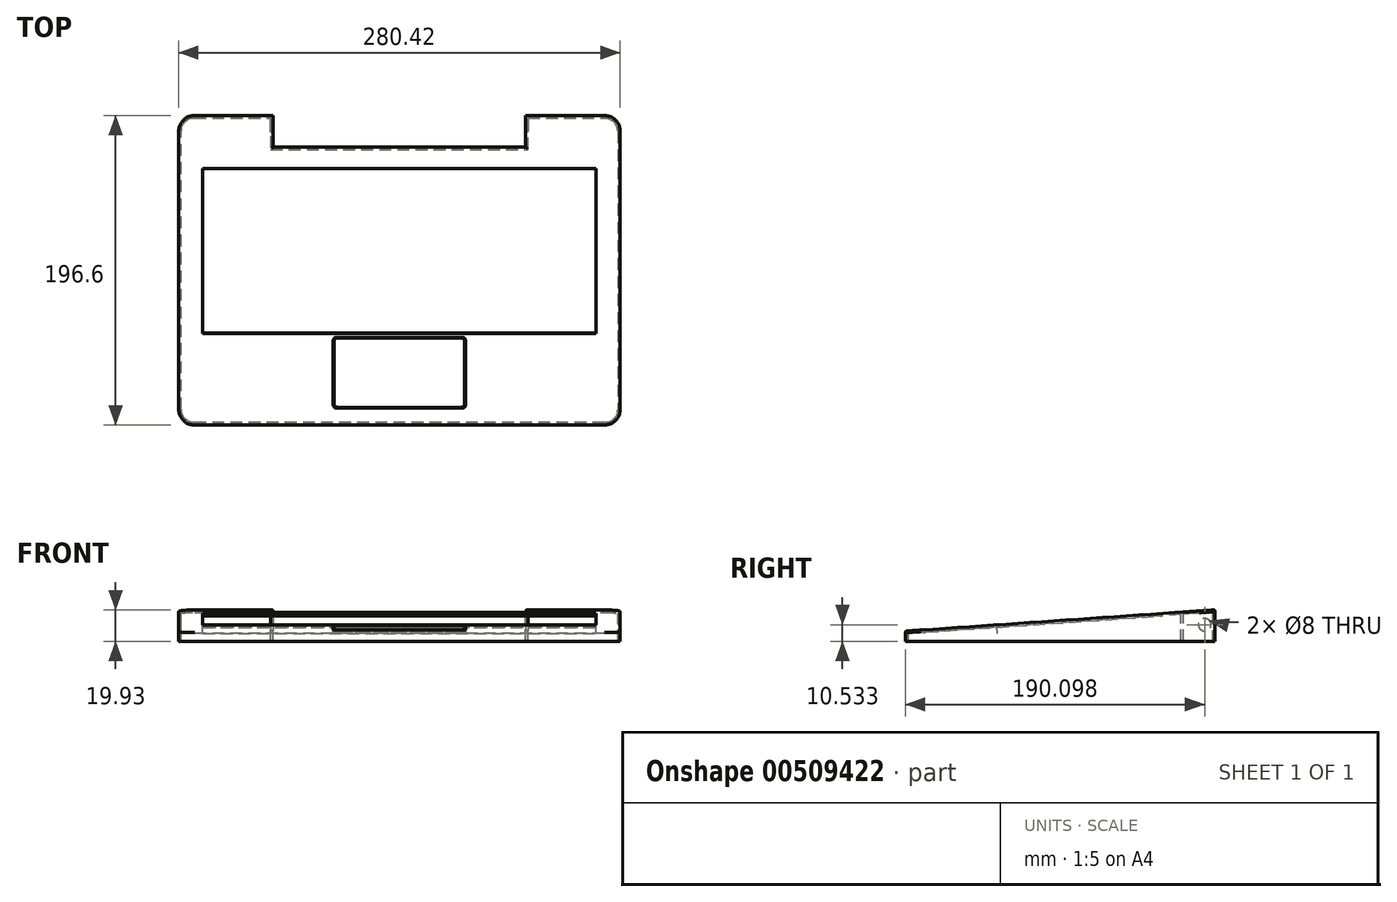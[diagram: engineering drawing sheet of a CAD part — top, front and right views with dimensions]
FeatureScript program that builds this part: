
annotation { "Feature Type Name" : "Feature", "Feature Type Description" : "" }
export const myFeature = defineFeature(function(context is Context, id is Id, definition is map)
    precondition{}
    {
        {
            var Q0;
            Q0=qCreatedBy(makeId("Right.planeOp"),FACE);
            cPlane(context, id + "F0", {"entities" : qUnion([Q0]), "cplaneType" : CPlaneType.OFFSET, "offset" : 140.2 * mm, "oppositeDirection" : true, "width" : 150 * mm, "height" : 150 * mm});
        }
        {
            var Q0;
            Q0=qCreatedBy(id+"F0.planeOp",FACE);
            var sketch = newSketch(context, id + "F1", { "sketchPlane" : qUnion([Q0])});
            skLineSegment(sketch, "E0.bottom", {"start": v(-98.3, -10) * mm, "end": v(98.3, -10) * mm});
            skLineSegment(sketch, "E0.right", {"start": v(98.3, -10) * mm, "end": v(98.3, 10) * mm});
            skPoint(sketch, "E0.middle", {"position": v(0, 0) * mm});
            skPoint(sketch, "E1", {"position": v(98.3, 0) * mm});
            skPoint(sketch, "E2", {"position": v(0, -10) * mm});
            skLineSegment(sketch, "E3", {"start": v(-98.3, -10) * mm, "end": v(-98.3, -3.5) * mm});
            skLineSegment(sketch, "E4", {"start": v(98.3, 10) * mm, "end": v(-98.3, -3.5) * mm});
            skSolve(sketch);
        }
        {
            var Q0;
            Q0=makeQuery(id+"F1.imprint","IMPRINT",FACE,{"disambiguationData":[TD([[makeQuery(id+"F1.imprint","IMPRINT",EDGE,{"derivedFrom":sQuery(id+"F1.wireOp",EDGE,"E0.bottom")}),1.0]])]});
            extrude(context, id + "F2", {"entities" : qUnion([Q0]), "depth" : 280.42 * mm, "offsetDistance" : 25 * mm});
        }
        {
            var Q0;
            Q0=makeQuery(id+"F2.opExtrude","CAP_EDGE",EDGE,{"disambiguationData":[OSD([sQuery(id+"F1.wireOp",EDGE,"E0.right")])],"isStart":true});
            var Q1;
            Q1=makeQuery(id+"F2.opExtrude","CAP_EDGE",EDGE,{"disambiguationData":[OSD([sQuery(id+"F1.wireOp",EDGE,"E3")])],"isStart":true});
            var Q2;
            Q2=makeQuery(id+"F2.opExtrude","CAP_EDGE",EDGE,{"disambiguationData":[OSD([sQuery(id+"F1.wireOp",EDGE,"E3")])],"isStart":false});
            var Q3;
            Q3=makeQuery(id+"F2.opExtrude","CAP_EDGE",EDGE,{"disambiguationData":[OSD([sQuery(id+"F1.wireOp",EDGE,"E0.right")])],"isStart":false});
            fillet(context, id + "F3", {"entities" : qUnion([Q0, Q1, Q2, Q3]), "radius" : 10 * mm, "tangentPropagation" : true, "allowEdgeOverflow" : false});
        }
        {
            var Q0;
            Q0=makeQuery(id+"F2.opExtrude","SWEPT_FACE",FACE,{"disambiguationData":[OSD([sQuery(id+"F1.wireOp",EDGE,"E0.bottom")])]});
            cPlane(context, id + "F4", {"entities" : qUnion([Q0]), "cplaneType" : CPlaneType.OFFSET, "offset" : 26.5 * mm, "oppositeDirection" : true, "width" : 150 * mm, "height" : 150 * mm});
        }
        {
            var Q0;
            Q0=qCreatedBy(id+"F4.planeOp",FACE);
            var sketch = newSketch(context, id + "F5", { "sketchPlane" : qUnion([Q0])});
            skPoint(sketch, "E5", {"position": v(-80.2, -98.3) * mm});
            skPoint(sketch, "E6", {"position": v(80.2, -98.3) * mm});
            skLineSegment(sketch, "E7.bottom", {"start": v(-80.2, -98.3) * mm, "end": v(80.2, -98.3) * mm});
            skLineSegment(sketch, "E7.top", {"start": v(-80.2, -78.3) * mm, "end": v(80.2, -78.3) * mm});
            skLineSegment(sketch, "E7.left", {"start": v(-80.2, -98.3) * mm, "end": v(-80.2, -78.3) * mm});
            skLineSegment(sketch, "E7.right", {"start": v(80.2, -98.3) * mm, "end": v(80.2, -78.3) * mm});
            skSolve(sketch);
        }
        {
            var Q0;
            Q0 = qSketchRegion(id + "F5", true);
            extrude(context, id + "F6", {"entities" : qUnion([Q0]), "operationType" : NewBodyOperationType.REMOVE, "depth" : 30 * mm, "offsetDistance" : 25 * mm});
        }
        {
            var Q0;
            Q0=makeQuery(id+"F2.opExtrude","SWEPT_FACE",FACE,{"disambiguationData":[OSD([sQuery(id+"F1.wireOp",EDGE,"E4")])]});
            fillet(context, id + "F7", {"entities" : qUnion([Q0]), "radius" : 1 * mm, "tangentPropagation" : true, "rho" : 0.5, "crossSection" : FilletCrossSection.CONIC, "allowEdgeOverflow" : false});
        }
        {
            var Q0;
            Q0=makeQuery(id+"F2.opExtrude","SWEPT_FACE",FACE,{"disambiguationData":[OSD([sQuery(id+"F1.wireOp",EDGE,"E0.bottom")])]});
            shell(context, id + "F8", {"entities" : qUnion([Q0]), "thickness" : 1.5 * mm});
        }
        {
            var Q0;
            Q0=makeQuery(id+"F2.opExtrude","SWEPT_FACE",FACE,{"disambiguationData":[OSD([sQuery(id+"F1.wireOp",EDGE,"E4")])]});
            var sketch = newSketch(context, id + "F9", { "sketchPlane" : qUnion([Q0])});
            skLineSegment(sketch, "E8.bottom", {"start": v(125, 65) * mm, "end": v(-125, 65) * mm});
            skPoint(sketch, "E8.middle", {"position": v(0, 0) * mm});
            skPoint(sketch, "E9", {"position": v(0, 65) * mm});
            skLineSegment(sketch, "E10", {"start": v(-125, 65) * mm, "end": v(-125, -40) * mm});
            skLineSegment(sketch, "E11", {"start": v(125, 65) * mm, "end": v(125, -40) * mm});
            skLineSegment(sketch, "E12", {"start": v(-125, -40) * mm, "end": v(125, -40) * mm});
            skPoint(sketch, "E13", {"position": v(0, 12.5) * mm});
            skPoint(sketch, "E13.positionSnap0", {"position": v(-125, 12.5) * mm});
            skSolve(sketch);
        }
        {
            var Q0;
            Q0=makeQuery(id+"F2.opExtrude","SWEPT_FACE",FACE,{"disambiguationData":[OSD([sQuery(id+"F1.wireOp",EDGE,"E4")])]});
            var sketch = newSketch(context, id + "F10", { "sketchPlane" : qUnion([Q0])});
            skPoint(sketch, "E14", {"position": v(0, -65) * mm});
            skLineSegment(sketch, "E15.bottom", {"start": v(40, -87.5) * mm, "end": v(-40, -87.5) * mm});
            skLineSegment(sketch, "E15.top", {"start": v(40, -42.5) * mm, "end": v(-40, -42.5) * mm});
            skLineSegment(sketch, "E15.left", {"start": v(42, -85.5) * mm, "end": v(42, -44.5) * mm});
            skLineSegment(sketch, "E15.right", {"start": v(-42, -85.5) * mm, "end": v(-42, -44.5) * mm});
            skPoint(sketch, "E16.visualSharp", {"position": v(-42, -42.5) * mm});
            skArc(sketch, "E16.filletArc", {"start": v(-40, -42.5) * mm, "mid": v(-41.41, -43.09) * mm, "end": v(-42, -44.5) * mm});
            skPoint(sketch, "E17.visualSharp", {"position": v(42, -42.5) * mm});
            skArc(sketch, "E17.filletArc", {"start": v(42, -44.5) * mm, "mid": v(41.41, -43.09) * mm, "end": v(40, -42.5) * mm});
            skPoint(sketch, "E18.visualSharp", {"position": v(42, -87.5) * mm});
            skArc(sketch, "E18.filletArc", {"start": v(40, -87.5) * mm, "mid": v(41.41, -86.91) * mm, "end": v(42, -85.5) * mm});
            skPoint(sketch, "E19.visualSharp", {"position": v(-42, -87.5) * mm});
            skArc(sketch, "E19.filletArc", {"start": v(-42, -85.5) * mm, "mid": v(-41.41, -86.91) * mm, "end": v(-40, -87.5) * mm});
            skSolve(sketch);
        }
        {
            var Q0;
            Q0 = qSketchRegion(id + "F10", true);
            extrude(context, id + "F11", {"entities" : qUnion([Q0]), "operationType" : NewBodyOperationType.REMOVE, "oppositeDirection" : true, "depth" : 5 * mm, "offsetDistance" : 25 * mm});
        }
        {
            var Q0;
            Q0=makeQuery(id+"F8.opShell","OFFSET_FACE",FACE,{"disambiguationData":[OSD([sQuery(id+"F1.wireOp",EDGE,"E4")])]});
            var sketch = newSketch(context, id + "F12", { "sketchPlane" : qUnion([Q0])});
            skPoint(sketch, "E20", {"position": v(0, 65) * mm});
            skLineSegment(sketch, "E21.bottom", {"start": v(39.5, 87) * mm, "end": v(-39.5, 87) * mm});
            skLineSegment(sketch, "E21.top", {"start": v(39.5, 43) * mm, "end": v(-39.5, 43) * mm});
            skLineSegment(sketch, "E21.left", {"start": v(41.5, 85) * mm, "end": v(41.5, 45) * mm});
            skLineSegment(sketch, "E21.right", {"start": v(-41.5, 85) * mm, "end": v(-41.5, 45) * mm});
            skPoint(sketch, "E22.visualSharp", {"position": v(-41.5, 43) * mm});
            skArc(sketch, "E22.filletArc", {"start": v(-41.5, 45) * mm, "mid": v(-40.91, 43.59) * mm, "end": v(-39.5, 43) * mm});
            skPoint(sketch, "E23.visualSharp", {"position": v(41.5, 43) * mm});
            skArc(sketch, "E23.filletArc", {"start": v(39.5, 43) * mm, "mid": v(40.91, 43.59) * mm, "end": v(41.5, 45) * mm});
            skPoint(sketch, "E24.visualSharp", {"position": v(41.5, 87) * mm});
            skArc(sketch, "E24.filletArc", {"start": v(41.5, 85) * mm, "mid": v(40.91, 86.41) * mm, "end": v(39.5, 87) * mm});
            skPoint(sketch, "E25.visualSharp", {"position": v(-41.5, 87) * mm});
            skArc(sketch, "E25.filletArc", {"start": v(-39.5, 87) * mm, "mid": v(-40.91, 86.41) * mm, "end": v(-41.5, 85) * mm});
            skSolve(sketch);
        }
        {
            var Q0;
            Q0 = qSketchRegion(id + "F12", true);
            extrude(context, id + "F13", {"entities" : qUnion([Q0]), "oppositeDirection" : true, "depth" : 1.25 * mm, "offsetDistance" : 25 * mm});
        }
        {
            var Q0;
            Q0=makeQuery(id+"F6.boolean.opBoolean","COPY",FACE,{"derivedFrom":makeQuery(id+"F6.opExtrude","SWEPT_FACE",FACE,{"disambiguationData":[OSD([sQuery(id+"F5.wireOp",EDGE,"E7.right")])]})});
            var sketch = newSketch(context, id + "F14", { "sketchPlane" : qUnion([Q0])});
            skCircle(sketch, "E26", {"center": v(-91.8, 0.53) * mm, "radius": 4 * mm});
            skSolve(sketch);
        }
        {
            var Q0;
            Q0 = qSketchRegion(id + "F14", true);
            extrude(context, id + "F15", {"entities" : qUnion([Q0]), "operationType" : NewBodyOperationType.REMOVE, "oppositeDirection" : true, "depth" : 20 * mm, "offsetDistance" : 25 * mm});
        }
        {
            var Q0;
            Q0 = qSketchRegion(id + "F14", true);
            extrude(context, id + "F16", {"entities" : qUnion([Q0]), "operationType" : NewBodyOperationType.REMOVE, "depth" : 180 * mm, "offsetDistance" : 25 * mm});
        }
        {
            var Q0;
            Q0 = qSketchRegion(id + "F9", true);
            extrude(context, id + "F17", {"entities" : qUnion([Q0]), "oppositeDirection" : true, "depth" : 4 * mm, "offsetDistance" : 25 * mm});
        }
        {
            var Q0;
            Q0=makeQuery(id+"F17.opExtrude","SWEPT_BODY",BODY,{"disambiguationData":[OSD([sQuery(id+"F9.wireOp",EDGE,"E8.bottom"),sQuery(id+"F9.wireOp",EDGE,"E10"),sQuery(id+"F9.wireOp",EDGE,"E11"),sQuery(id+"F9.wireOp",EDGE,"E12")])]});
            transform(context, id + "F18", {"entities" : qUnion([Q0]), "transformType" : TransformType.TRANSLATION_3D, "dx" : 0 * mm, "dy" : 0 * mm, "dz" : -1.5 * mm, "makeCopy" : false});
        }
        {
            var Q0;
            Q0 = qSketchRegion(id + "F9", true);
            extrude(context, id + "F19", {"entities" : qUnion([Q0]), "operationType" : NewBodyOperationType.REMOVE, "oppositeDirection" : true, "depth" : 25 * mm, "offsetDistance" : 25 * mm});
        }
    });
